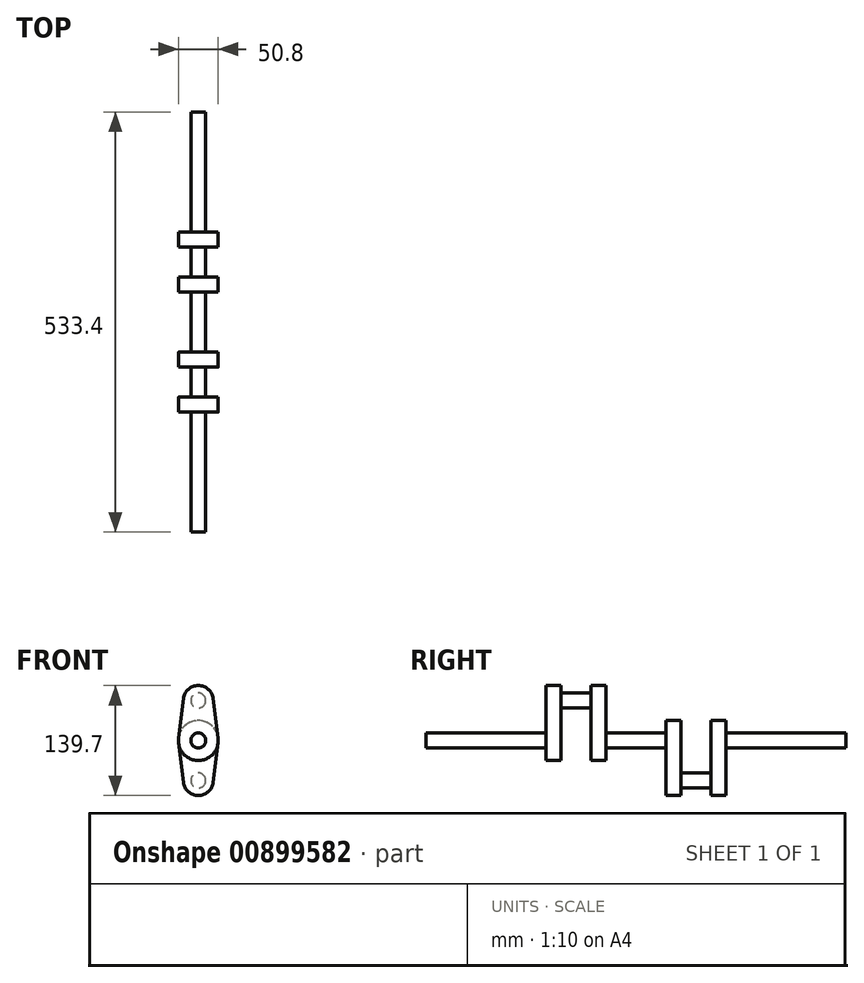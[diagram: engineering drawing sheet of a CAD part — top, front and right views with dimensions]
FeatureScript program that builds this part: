
annotation { "Feature Type Name" : "Feature", "Feature Type Description" : "" }
export const myFeature = defineFeature(function(context is Context, id is Id, definition is map)
    precondition{}
    {
        {
            var Q0;
            Q0=qCreatedBy(makeId("Front.planeOp"),FACE);
            var sketch = newSketch(context, id + "F0", { "sketchPlane" : qUnion([Q0])});
            skCircle(sketch, "E0", {"center": v(0, 0) * mm, "radius": 9.53 * mm});
            skSolve(sketch);
        }
        {
            var Q0;
            Q0 = qSketchRegion(id + "F0", true);
            extrude(context, id + "F1", {"entities" : qUnion([Q0]), "depth" : 152.4 * mm, "offsetDistance" : 25.4 * mm});
        }
        {
            var Q0;
            Q0=makeQuery(id+"F1.opExtrude","CAP_FACE",FACE,{"disambiguationData":[OSD([sQuery(id+"F0.wireOp",EDGE,"E0")])],"isStart":true});
            var sketch = newSketch(context, id + "F2", { "sketchPlane" : qUnion([Q0])});
            skCircle(sketch, "E1", {"center": v(0, 50.8) * mm, "radius": 19.05 * mm});
            skCircle(sketch, "E2", {"center": v(0, 50.8) * mm, "radius": 9.53 * mm});
            skCircle(sketch, "E3", {"center": v(0, 0) * mm, "radius": 25.4 * mm});
            skLineSegment(sketch, "E4", {"start": v(-15.99, 76.3) * mm, "end": v(-35.29, -76.87) * mm});
            skLineSegment(sketch, "E5", {"start": v(16.05, 75.8) * mm, "end": v(35.78, -80.77) * mm});
            skSolve(sketch);
        }
        {
            var Q0;
            Q0 = qSketchRegion(id + "F2", true);
            var Q1;
            Q1=makeQuery(id+"F2.imprint","IMPRINT",FACE,{"disambiguationData":[TD([[makeQuery(id+"F2.imprint","IMPRINT",EDGE,{"derivedFrom":sQuery(id+"F2.wireOp",EDGE,"E2")}),1.0]])]});
            extrude(context, id + "F3", {"entities" : qUnion([Q0, Q1]), "operationType" : NewBodyOperationType.ADD, "depth" : 19.05 * mm, "offsetDistance" : 25.4 * mm});
        }
        {
            var Q0;
            Q0=makeQuery(id+"F3.opExtrude","CAP_FACE",FACE,{"disambiguationData":[OSD([sQuery(id+"F2.wireOp",EDGE,"E1"),sQuery(id+"F2.wireOp",EDGE,"E3"),sQuery(id+"F2.wireOp",EDGE,"E4"),sQuery(id+"F2.wireOp",EDGE,"E5")])],"isStart":false});
            var sketch = newSketch(context, id + "F4", { "sketchPlane" : qUnion([Q0])});
            skCircle(sketch, "E6", {"center": v(0, 50.8) * mm, "radius": 9.53 * mm});
            skSolve(sketch);
        }
        {
            var Q0;
            Q0 = qSketchRegion(id + "F4", true);
            extrude(context, id + "F5", {"entities" : qUnion([Q0]), "operationType" : NewBodyOperationType.ADD, "depth" : 38.1 * mm, "offsetDistance" : 25.4 * mm});
        }
        {
            var Q0;
            Q0=makeQuery(id+"F5.opExtrude","CAP_FACE",FACE,{"disambiguationData":[OSD([sQuery(id+"F4.wireOp",EDGE,"E6")])],"isStart":false});
            var sketch = newSketch(context, id + "F6", { "sketchPlane" : qUnion([Q0])});
            skCircle(sketch, "E7", {"center": v(0, 50.8) * mm, "radius": 19.05 * mm});
            skCircle(sketch, "E8", {"center": v(0, 0) * mm, "radius": 25.4 * mm});
            skLineSegment(sketch, "E9", {"start": v(-16.62, 71.31) * mm, "end": v(-33.63, -63.71) * mm});
            skLineSegment(sketch, "E10", {"start": v(16.6, 71.51) * mm, "end": v(34.14, -67.8) * mm});
            skSolve(sketch);
        }
        {
            var Q0;
            Q0 = qSketchRegion(id + "F6", true);
            extrude(context, id + "F7", {"entities" : qUnion([Q0]), "operationType" : NewBodyOperationType.ADD, "depth" : 19.05 * mm, "offsetDistance" : 25.4 * mm});
        }
        {
            var Q0;
            Q0=makeQuery(id+"F7.opExtrude","CAP_FACE",FACE,{"disambiguationData":[OSD([sQuery(id+"F6.wireOp",EDGE,"E7"),sQuery(id+"F6.wireOp",EDGE,"E8"),sQuery(id+"F6.wireOp",EDGE,"E9"),sQuery(id+"F6.wireOp",EDGE,"E10")])],"isStart":false});
            var sketch = newSketch(context, id + "F8", { "sketchPlane" : qUnion([Q0])});
            skCircle(sketch, "E11", {"center": v(0, 0) * mm, "radius": 9.53 * mm});
            skSolve(sketch);
        }
        {
            var Q0;
            Q0 = qSketchRegion(id + "F8", true);
            extrude(context, id + "F9", {"entities" : qUnion([Q0]), "operationType" : NewBodyOperationType.ADD, "depth" : 76.2 * mm, "offsetDistance" : 25.4 * mm});
        }
        {
            var Q0;
            Q0=makeQuery(id+"F9.opExtrude","CAP_FACE",FACE,{"disambiguationData":[OSD([sQuery(id+"F8.wireOp",EDGE,"E11")])],"isStart":false});
            var sketch = newSketch(context, id + "F10", { "sketchPlane" : qUnion([Q0])});
            skCircle(sketch, "E12", {"center": v(0, 0) * mm, "radius": 25.4 * mm});
            skCircle(sketch, "E13", {"center": v(0, -50.8) * mm, "radius": 19.05 * mm});
            skLineSegment(sketch, "E14", {"start": v(-33.44, 62.22) * mm, "end": v(-15.93, -76.78) * mm});
            skLineSegment(sketch, "E15", {"start": v(32.8, 57.2) * mm, "end": v(16.68, -70.83) * mm});
            skSolve(sketch);
        }
        {
            var Q0;
            Q0 = qSketchRegion(id + "F10", true);
            extrude(context, id + "F11", {"entities" : qUnion([Q0]), "operationType" : NewBodyOperationType.ADD, "depth" : 19.05 * mm, "offsetDistance" : 25.4 * mm});
        }
        {
            var Q0;
            Q0=makeQuery(id+"F11.opExtrude","CAP_FACE",FACE,{"disambiguationData":[OSD([sQuery(id+"F10.wireOp",EDGE,"E12"),sQuery(id+"F10.wireOp",EDGE,"E13"),sQuery(id+"F10.wireOp",EDGE,"E14"),sQuery(id+"F10.wireOp",EDGE,"E15")])],"isStart":false});
            var sketch = newSketch(context, id + "F12", { "sketchPlane" : qUnion([Q0])});
            skCircle(sketch, "E16", {"center": v(0, -50.8) * mm, "radius": 9.53 * mm});
            skSolve(sketch);
        }
        {
            var Q0;
            Q0 = qSketchRegion(id + "F12", true);
            extrude(context, id + "F13", {"entities" : qUnion([Q0]), "operationType" : NewBodyOperationType.ADD, "depth" : 38.1 * mm, "offsetDistance" : 25.4 * mm});
        }
        {
            var Q0;
            Q0=makeQuery(id+"F13.opExtrude","CAP_FACE",FACE,{"disambiguationData":[OSD([sQuery(id+"F12.wireOp",EDGE,"E16")])],"isStart":false});
            var sketch = newSketch(context, id + "F14", { "sketchPlane" : qUnion([Q0])});
            skCircle(sketch, "E17", {"center": v(0, -50.8) * mm, "radius": 19.05 * mm});
            skCircle(sketch, "E18", {"center": v(0, 0) * mm, "radius": 25.4 * mm});
            skLineSegment(sketch, "E19", {"start": v(34.23, 68.48) * mm, "end": v(17.37, -65.3) * mm});
            skLineSegment(sketch, "E20", {"start": v(-33.23, 60.56) * mm, "end": v(-17.53, -64.1) * mm});
            skSolve(sketch);
        }
        {
            var Q0;
            Q0 = qSketchRegion(id + "F14", true);
            extrude(context, id + "F15", {"entities" : qUnion([Q0]), "operationType" : NewBodyOperationType.ADD, "depth" : 19.05 * mm, "offsetDistance" : 25.4 * mm});
        }
        {
            var Q0;
            Q0=makeQuery(id+"F15.opExtrude","CAP_FACE",FACE,{"disambiguationData":[OSD([sQuery(id+"F14.wireOp",EDGE,"E17"),sQuery(id+"F14.wireOp",EDGE,"E18"),sQuery(id+"F14.wireOp",EDGE,"E19"),sQuery(id+"F14.wireOp",EDGE,"E20")])],"isStart":false});
            var sketch = newSketch(context, id + "F16", { "sketchPlane" : qUnion([Q0])});
            skCircle(sketch, "E21", {"center": v(0, 0) * mm, "radius": 9.53 * mm});
            skSolve(sketch);
        }
        {
            var Q0;
            Q0 = qSketchRegion(id + "F16", true);
            extrude(context, id + "F17", {"entities" : qUnion([Q0]), "operationType" : NewBodyOperationType.ADD, "depth" : 152.4 * mm, "offsetDistance" : 25.4 * mm});
        }
    });
